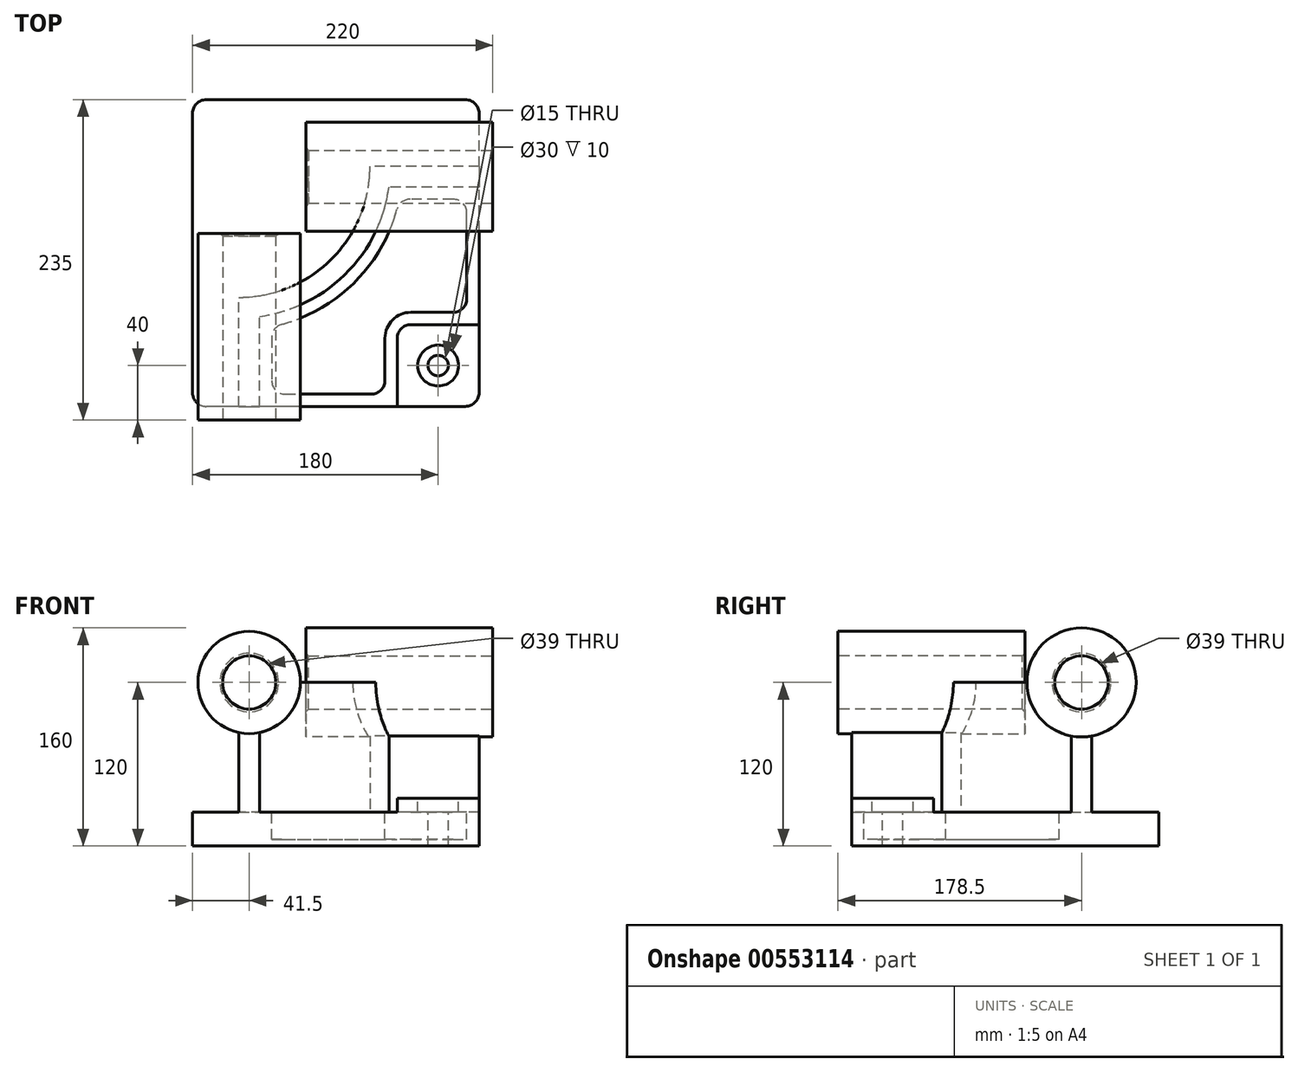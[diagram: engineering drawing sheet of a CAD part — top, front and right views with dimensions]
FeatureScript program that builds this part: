
annotation { "Feature Type Name" : "Feature", "Feature Type Description" : "" }
export const myFeature = defineFeature(function(context is Context, id is Id, definition is map)
    precondition{}
    {
        {
            var Q0;
            Q0=qCreatedBy(makeId("Top.planeOp"),FACE);
            var sketch = newSketch(context, id + "F0", { "sketchPlane" : qUnion([Q0])});
            skPoint(sketch, "E0.middle", {"position": v(0, 0) * mm});
            skLineSegment(sketch, "E1.bottom", {"start": v(105, -112.5) * mm, "end": v(-105, -112.5) * mm});
            skLineSegment(sketch, "E1.top", {"start": v(105, 112.5) * mm, "end": v(-105, 112.5) * mm});
            skLineSegment(sketch, "E1.left", {"start": v(105, -112.5) * mm, "end": v(105, 112.5) * mm});
            skLineSegment(sketch, "E1.right", {"start": v(-105, -112.5) * mm, "end": v(-105, 112.5) * mm});
            skSolve(sketch);
        }
        {
            var Q0;
            Q0=makeQuery(id+"F0.imprint","IMPRINT",FACE,{"disambiguationData":[TD([[makeQuery(id+"F0.imprint","IMPRINT",EDGE,{"derivedFrom":sQuery(id+"F0.wireOp",EDGE,"E1.bottom")}),-1.0]])]});
            extrude(context, id + "F1", {"entities" : qUnion([Q0]), "depth" : 25 * mm, "offsetDistance" : 25 * mm});
        }
        {
            var Q0;
            Q0=makeQuery(id+"F1.opExtrude","CAP_FACE",FACE,{"disambiguationData":[OSD([sQuery(id+"F0.wireOp",EDGE,"E1.bottom"),sQuery(id+"F0.wireOp",EDGE,"E1.top"),sQuery(id+"F0.wireOp",EDGE,"E1.left"),sQuery(id+"F0.wireOp",EDGE,"E1.right")])],"isStart":false});
            var sketch = newSketch(context, id + "F2", { "sketchPlane" : qUnion([Q0])});
            skLineSegment(sketch, "E2", {"start": v(-71, -112.5) * mm, "end": v(-71, -32.5) * mm});
            skLineSegment(sketch, "E3", {"start": v(105, 63.5) * mm, "end": v(25, 63.5) * mm});
            skArc(sketch, "E4", {"start": v(-71, -32.5) * mm, "mid": v(-3.12, -4.38) * mm, "end": v(25, 63.5) * mm});
            skLineSegment(sketch, "E5", {"start": v(-71, 63.5) * mm, "end": v(25, 63.5) * mm, "construction": true});
            skLineSegment(sketch, "E6", {"start": v(-71, 63.5) * mm, "end": v(-71, -32.5) * mm, "construction": true});
            skLineSegment(sketch, "E7.0", {"start": v(-56, -112.5) * mm, "end": v(-56, -46.48) * mm});
            skArc(sketch, "E7.1", {"start": v(-56, -46.48) * mm, "mid": v(7.49, -14.99) * mm, "end": v(38.98, 48.5) * mm});
            skLineSegment(sketch, "E7.2", {"start": v(105, 48.5) * mm, "end": v(38.98, 48.5) * mm});
            skLineSegment(sketch, "E8.0", {"start": v(105, -112.5) * mm, "end": v(105, 112.5) * mm});
            skLineSegment(sketch, "E9.0", {"start": v(105, -112.5) * mm, "end": v(-105, -112.5) * mm});
            skSolve(sketch);
        }
        {
            var Q0;
            {var subQ2=sQuery(id+"F2.wireOp",EDGE,"E2");Q0=makeQuery(id+"F2.imprint","IMPRINT",FACE,{"disambiguationData":[TD([[makeQuery(id+"F2.imprint","IMPRINT",EDGE,{"derivedFrom":subQ2}),-1.0]])]});}
            extrude(context, id + "F3", {"entities" : qUnion([Q0]), "operationType" : NewBodyOperationType.ADD, "depth" : 95 * mm, "offsetDistance" : 25 * mm});
        }
        {
            var Q0;
            Q0=makeQuery(id+"F3.boolean.opBoolean","MERGE",FACE,{"derivedFrom":[makeQuery(id+"F1.opExtrude","SWEPT_FACE",FACE,{"disambiguationData":[OSD([sQuery(id+"F0.wireOp",EDGE,"E1.bottom")])]}),makeQuery(id+"F3.opExtrude","SWEPT_FACE",FACE,{"disambiguationData":[OSD([sQuery(id+"F2.wireOp",EDGE,"E9.0")])]})]});
            var sketch = newSketch(context, id + "F4", { "sketchPlane" : qUnion([Q0])});
            skCircle(sketch, "E10", {"center": v(-63.5, 120) * mm, "radius": 37.5 * mm});
            skSolve(sketch);
        }
        {
            var Q0;
            Q0 = qSketchRegion(id + "F4", true);
            extrude(context, id + "F5", {"entities" : qUnion([Q0]), "operationType" : NewBodyOperationType.ADD, "depth" : 10 * mm, "offsetDistance" : 25 * mm, "hasSecondDirection" : true, "secondDirectionOppositeDirection" : true, "secondDirectionDepth" : (137 - 10) * mm});
        }
        {
            var Q0;
            Q0=makeQuery(id+"F3.boolean.opBoolean","MERGE",FACE,{"derivedFrom":[makeQuery(id+"F1.opExtrude","SWEPT_FACE",FACE,{"disambiguationData":[OSD([sQuery(id+"F0.wireOp",EDGE,"E1.left")])]}),makeQuery(id+"F3.opExtrude","SWEPT_FACE",FACE,{"disambiguationData":[OSD([sQuery(id+"F2.wireOp",EDGE,"E8.0")])]})]});
            var sketch = newSketch(context, id + "F6", { "sketchPlane" : qUnion([Q0])});
            skCircle(sketch, "E11", {"center": v(56, 120) * mm, "radius": 40 * mm});
            skSolve(sketch);
        }
        {
            var Q0;
            Q0 = qSketchRegion(id + "F6", true);
            extrude(context, id + "F7", {"entities" : qUnion([Q0]), "operationType" : NewBodyOperationType.ADD, "depth" : 10 * mm, "offsetDistance" : 25 * mm, "hasSecondDirection" : true, "secondDirectionOppositeDirection" : true, "secondDirectionDepth" : (137 - 10) * mm});
        }
        {
            var Q0;
            {var subQ0=sQuery(id+"F0.wireOp",EDGE,"E1.left");var subQ1=sQuery(id+"F0.wireOp",EDGE,"E1.bottom");Q0=makeQuery(id+"F3.boolean.opBoolean","SPLIT",FACE,{"disambiguationData":[TD([makeQuery(id+"F3.opExtrude","SWEPT_FACE",FACE,{"disambiguationData":[OSD([sQuery(id+"F2.wireOp",EDGE,"E7.0")])]})])],"derivedFrom":makeQuery(id+"F1.opExtrude","CAP_FACE",FACE,{"disambiguationData":[OSD([subQ1,sQuery(id+"F0.wireOp",EDGE,"E1.top"),subQ0,sQuery(id+"F0.wireOp",EDGE,"E1.right")])],"isStart":false})});}
            var sketch = newSketch(context, id + "F8", { "sketchPlane" : qUnion([Q0])});
            skLineSegment(sketch, "E12.bottom", {"start": v(105, -112.5) * mm, "end": v(45, -112.5) * mm});
            skLineSegment(sketch, "E12.top", {"start": v(105, -52.5) * mm, "end": v(45, -52.5) * mm});
            skLineSegment(sketch, "E12.left", {"start": v(105, -112.5) * mm, "end": v(105, -52.5) * mm});
            skLineSegment(sketch, "E12.right", {"start": v(45, -112.5) * mm, "end": v(45, -52.5) * mm});
            skSolve(sketch);
        }
        {
            var Q0;
            Q0 = qSketchRegion(id + "F8", true);
            extrude(context, id + "F9", {"entities" : qUnion([Q0]), "operationType" : NewBodyOperationType.ADD, "depth" : (35 - 25) * mm, "offsetDistance" : 25 * mm});
        }
        {
            var Q0;
            Q0=makeQuery(id+"F9.opExtrude","SWEPT_EDGE",EDGE,{"disambiguationData":[OSD([sQuery(id+"F8.wireOp",EDGE,"E12.top"),sQuery(id+"F8.wireOp",EDGE,"E12.right")])]});
            fillet(context, id + "F10", {"entities" : qUnion([Q0]), "radius" : 10 * mm, "tangentPropagation" : true, "allowEdgeOverflow" : false});
        }
        {
            var Q0;
            {var subQ0=sQuery(id+"F0.wireOp",EDGE,"E1.left");var subQ1=sQuery(id+"F0.wireOp",EDGE,"E1.bottom");Q0=makeQuery(id+"F3.boolean.opBoolean","SPLIT",FACE,{"disambiguationData":[TD([makeQuery(id+"F3.opExtrude","SWEPT_FACE",FACE,{"disambiguationData":[OSD([sQuery(id+"F2.wireOp",EDGE,"E7.0")])]})])],"derivedFrom":makeQuery(id+"F1.opExtrude","CAP_FACE",FACE,{"disambiguationData":[OSD([subQ1,sQuery(id+"F0.wireOp",EDGE,"E1.top"),subQ0,sQuery(id+"F0.wireOp",EDGE,"E1.right")])],"isStart":false})});}
            var sketch = newSketch(context, id + "F11", { "sketchPlane" : qUnion([Q0])});
            skLineSegment(sketch, "E13.0", {"start": v(-47, -54.08) * mm, "end": v(-47, -103.5) * mm});
            skArc(sketch, "E13.1", {"start": v(46.58, 39.5) * mm, "mid": v(13.85, -21.35) * mm, "end": v(-47, -54.08) * mm});
            skLineSegment(sketch, "E13.2", {"start": v(-47, -103.5) * mm, "end": v(36, -103.5) * mm});
            skLineSegment(sketch, "E13.3", {"start": v(96, 39.5) * mm, "end": v(46.58, 39.5) * mm});
            skLineSegment(sketch, "E13.4", {"start": v(36, -103.5) * mm, "end": v(36, -62.5) * mm});
            skArc(sketch, "E13.5", {"start": v(36, -62.5) * mm, "mid": v(41.56, -49.06) * mm, "end": v(55, -43.5) * mm});
            skLineSegment(sketch, "E13.6", {"start": v(55, -43.5) * mm, "end": v(96, -43.5) * mm});
            skLineSegment(sketch, "E13.7", {"start": v(96, -43.5) * mm, "end": v(96, 39.5) * mm});
            skSolve(sketch);
        }
        {
            var Q0;
            Q0=makeQuery(id+"F11.imprint","IMPRINT",FACE,{"disambiguationData":[TD([[makeQuery(id+"F11.imprint","IMPRINT",EDGE,{"derivedFrom":sQuery(id+"F11.wireOp",EDGE,"E13.0")}),1.0]])]});
            extrude(context, id + "F12", {"entities" : qUnion([Q0]), "operationType" : NewBodyOperationType.REMOVE, "oppositeDirection" : true, "depth" : (25 - 5) * mm, "offsetDistance" : 25 * mm});
        }
        {
            var Q0;
            Q0=makeQuery(id+"F9.opExtrude","CAP_FACE",FACE,{"disambiguationData":[OSD([sQuery(id+"F8.wireOp",EDGE,"E12.bottom"),sQuery(id+"F8.wireOp",EDGE,"E12.top"),sQuery(id+"F8.wireOp",EDGE,"E12.left"),sQuery(id+"F8.wireOp",EDGE,"E12.right")])],"isStart":false});
            var sketch = newSketch(context, id + "F13", { "sketchPlane" : qUnion([Q0])});
            skCircle(sketch, "E14", {"center": v(75, -82.5) * mm, "radius": 15 * mm});
            skPoint(sketch, "E14.centerSnap0", {"position": v(75, -112.5) * mm});
            skSolve(sketch);
        }
        {
            var Q0;
            Q0=sQuery(id+"F13.wireOp",VERTEX,"E14.center");
            var Q1;
            Q1=makeQuery(id+"F1.opExtrude","SWEPT_BODY",BODY,{"disambiguationData":[OSD([sQuery(id+"F0.wireOp",EDGE,"E1.bottom"),sQuery(id+"F0.wireOp",EDGE,"E1.top"),sQuery(id+"F0.wireOp",EDGE,"E1.left"),sQuery(id+"F0.wireOp",EDGE,"E1.right")])]});
            hole(context, id + "F14", {"style" : HoleStyle.C_BORE, "endStyle" : HoleEndStyle.THROUGH, "holeDiameter" : 15 * mm, "cBoreDiameter" : 30 * mm, "cBoreDepth" : 10 * mm, "isTappedThrough" : true, "tappedDepth" : 12 * mm, "tapClearance" : 3, "locations" : qUnion([Q0]), "scope" : qUnion([Q1])});
        }
        {
            var Q0;
            Q0=makeQuery(id+"F12.boolean.opBoolean","COPY",EDGE,{"derivedFrom":makeQuery(id+"F12.opExtrude","SWEPT_EDGE",EDGE,{"disambiguationData":[OSD([sQuery(id+"F11.wireOp",EDGE,"E13.1"),sQuery(id+"F11.wireOp",EDGE,"E13.3")])]})});
            var Q1;
            Q1=makeQuery(id+"F12.boolean.opBoolean","COPY",EDGE,{"derivedFrom":makeQuery(id+"F12.opExtrude","SWEPT_EDGE",EDGE,{"disambiguationData":[OSD([sQuery(id+"F11.wireOp",EDGE,"E13.0"),sQuery(id+"F11.wireOp",EDGE,"E13.1")])]})});
            var Q2;
            Q2=makeQuery(id+"F12.boolean.opBoolean","COPY",EDGE,{"derivedFrom":makeQuery(id+"F12.opExtrude","SWEPT_EDGE",EDGE,{"disambiguationData":[OSD([sQuery(id+"F11.wireOp",EDGE,"E13.3"),sQuery(id+"F11.wireOp",EDGE,"E13.7")])]})});
            var Q3;
            Q3=makeQuery(id+"F12.boolean.opBoolean","COPY",EDGE,{"derivedFrom":makeQuery(id+"F12.opExtrude","SWEPT_EDGE",EDGE,{"disambiguationData":[OSD([sQuery(id+"F11.wireOp",EDGE,"E13.6"),sQuery(id+"F11.wireOp",EDGE,"E13.7")])]})});
            var Q4;
            Q4=makeQuery(id+"F12.boolean.opBoolean","COPY",EDGE,{"derivedFrom":makeQuery(id+"F12.opExtrude","SWEPT_EDGE",EDGE,{"disambiguationData":[OSD([sQuery(id+"F11.wireOp",EDGE,"E13.2"),sQuery(id+"F11.wireOp",EDGE,"E13.4")])]})});
            var Q5;
            Q5=makeQuery(id+"F12.boolean.opBoolean","COPY",EDGE,{"derivedFrom":makeQuery(id+"F12.opExtrude","SWEPT_EDGE",EDGE,{"disambiguationData":[OSD([sQuery(id+"F11.wireOp",EDGE,"E13.0"),sQuery(id+"F11.wireOp",EDGE,"E13.2")])]})});
            fillet(context, id + "F15", {"entities" : qUnion([Q0, Q1, Q2, Q3, Q4, Q5]), "radius" : 10 * mm, "tangentPropagation" : true, "allowEdgeOverflow" : false});
        }
        {
            var Q0;
            Q0=makeQuery(id+"F5.opExtrude","CAP_FACE",FACE,{"disambiguationData":[OSD([sQuery(id+"F4.wireOp",EDGE,"E10")])],"isStart":false});
            var sketch = newSketch(context, id + "F16", { "sketchPlane" : qUnion([Q0])});
            skCircle(sketch, "E15", {"center": v(-63.5, 120) * mm, "radius": 19.5 * mm});
            skSolve(sketch);
        }
        {
            var Q0;
            Q0 = qSketchRegion(id + "F16", true);
            extrude(context, id + "F17", {"entities" : qUnion([Q0]), "operationType" : NewBodyOperationType.REMOVE, "endBound" : BoundingType.THROUGH_ALL, "oppositeDirection" : true, "depth" : 25 * mm, "offsetDistance" : 25 * mm});
        }
        {
            var Q0;
            Q0=makeQuery(id+"F7.opExtrude","CAP_FACE",FACE,{"disambiguationData":[OSD([sQuery(id+"F6.wireOp",EDGE,"E11")])],"isStart":false});
            var sketch = newSketch(context, id + "F18", { "sketchPlane" : qUnion([Q0])});
            skCircle(sketch, "E16", {"center": v(56, 120) * mm, "radius": 19.5 * mm});
            skSolve(sketch);
        }
        {
            var Q0;
            Q0 = qSketchRegion(id + "F18", true);
            extrude(context, id + "F19", {"entities" : qUnion([Q0]), "operationType" : NewBodyOperationType.REMOVE, "endBound" : BoundingType.THROUGH_ALL, "oppositeDirection" : true, "depth" : 25 * mm, "offsetDistance" : 25 * mm});
        }
        {
            var Q0;
            Q0=makeQuery(id+"F17.boolean.opBoolean","COPY",EDGE,{"derivedFrom":makeQuery(id+"F17.opExtrude","CAP_EDGE",EDGE,{"disambiguationData":[OSD([sQuery(id+"F16.wireOp",EDGE,"E15")])],"isStart":true})});
            var Q1;
            Q1=makeQuery(id+"F19.boolean.opBoolean","COPY",EDGE,{"derivedFrom":makeQuery(id+"F19.opExtrude","CAP_EDGE",EDGE,{"disambiguationData":[OSD([sQuery(id+"F18.wireOp",EDGE,"E16")])],"isStart":true})});
            var Q2;
            Q2=makeQuery(id+"F19.boolean.opBoolean","INTERSECT",EDGE,{"derivedFrom":[makeQuery(id+"F7.opExtrude","CAP_FACE",FACE,{"disambiguationData":[OSD([sQuery(id+"F6.wireOp",EDGE,"E11")])],"isStart":true}),makeQuery(id+"F19.opExtrude","SWEPT_FACE",FACE,{"disambiguationData":[OSD([sQuery(id+"F18.wireOp",EDGE,"E16")])]})]});
            var Q3;
            Q3=makeQuery(id+"F17.boolean.opBoolean","INTERSECT",EDGE,{"derivedFrom":[makeQuery(id+"F5.opExtrude","CAP_FACE",FACE,{"disambiguationData":[OSD([sQuery(id+"F4.wireOp",EDGE,"E10")])],"isStart":true}),makeQuery(id+"F17.opExtrude","SWEPT_FACE",FACE,{"disambiguationData":[OSD([sQuery(id+"F16.wireOp",EDGE,"E15")])]})]});
            chamfer(context, id + "F20", {"entities" : qUnion([Q0, Q1, Q2, Q3]), "width" : 2 * mm, "tangentPropagation" : true});
        }
        {
            var Q0;
            Q0=makeQuery(id+"F1.opExtrude","SWEPT_EDGE",EDGE,{"disambiguationData":[OSD([sQuery(id+"F0.wireOp",EDGE,"E1.bottom"),sQuery(id+"F0.wireOp",EDGE,"E1.right")])]});
            var Q1;
            Q1=makeQuery(id+"F9.boolean.opBoolean","MERGE",EDGE,{"derivedFrom":[makeQuery(id+"F1.opExtrude","SWEPT_EDGE",EDGE,{"disambiguationData":[OSD([sQuery(id+"F0.wireOp",EDGE,"E1.bottom"),sQuery(id+"F0.wireOp",EDGE,"E1.left")])]}),makeQuery(id+"F9.opExtrude","SWEPT_EDGE",EDGE,{"disambiguationData":[OSD([sQuery(id+"F8.wireOp",EDGE,"E12.bottom"),sQuery(id+"F8.wireOp",EDGE,"E12.left")])]})]});
            var Q2;
            Q2=makeQuery(id+"F1.opExtrude","SWEPT_EDGE",EDGE,{"disambiguationData":[OSD([sQuery(id+"F0.wireOp",EDGE,"E1.top"),sQuery(id+"F0.wireOp",EDGE,"E1.left")])]});
            var Q3;
            Q3=makeQuery(id+"F1.opExtrude","SWEPT_EDGE",EDGE,{"disambiguationData":[OSD([sQuery(id+"F0.wireOp",EDGE,"E1.top"),sQuery(id+"F0.wireOp",EDGE,"E1.right")])]});
            fillet(context, id + "F21", {"entities" : qUnion([Q0, Q1, Q2, Q3]), "radius" : 10 * mm, "tangentPropagation" : true, "allowEdgeOverflow" : false});
        }
    });
